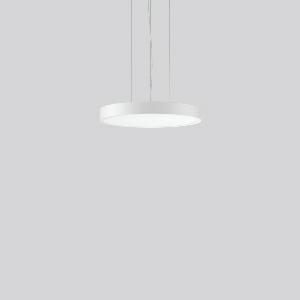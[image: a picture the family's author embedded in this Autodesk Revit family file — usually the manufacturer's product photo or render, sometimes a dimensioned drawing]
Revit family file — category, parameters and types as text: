
# Revit family: triona_round_p_312422_002_730_0688
name_source: partatom
category: Lighting Fixtures
units: mm (PartAtom-declared; Revit-internal decimal feet)

## family parameters
Cut with Voids When Loaded = No
Host = Face
Light Source = No
Part Type = Normal
Room Calculation Point = No
Round Connector Dimension = Use Diameter
Shared = No

## types (1)
- TRIONA round P (1 x LED Modul 830, 5850 lm, 3000)
    Apparent Load = 64 VA
    CIE Flux Codes = 49 80 96 82 100
    Color Rendering = 80
    Color Temperature = 3000
    Default Elevation = 1800 mm
    Description = Series: TRIONA round
Decorative round LED pendant-mounted surface luminaire. Flat, seamless frame: aluminium extrusion profile, powder coated. Cover made of sheet steel, powder-coated. Canopy made of aluminium, powder-coated. Direct light emission through a diffuser plastic opal. Indirect light emission through a flush diffuser made of satin-finish plastic. Lightguide and diffuser made of non-yellowing plastic (PMMA). Lateral light emission (RZB SIDELITE technology) for above-average homogeneous light distribution. Direct 70%, indirect 30% light emission. 3-point steel cable suspension, steplessly adjustable. Easy installation with transparent, adjustable pendant cable and canopy with magnetic fixing. Driver integrated. 
Colour: traffic white, matt (RAL 9016)
Diameter: 461 mm
Height: 52 mm
Suspension length: 500-1200 mm
Lamp: LED
Socket: without socket
Colour temperature: 3000K
Colour rendering index (CRI): 80
System power: 64 W
Rated luminous flux: 5850 lm
Luminous efficiency: 91 lm/W
Control gear: Dimmable Bluetooth converter
Protection class: I
Type of protection: IP 20
    Height = 52 mm  [stored 0.170604 ft]
    Lamp = 1 x LED Modul 830
    Lamp Light Flux = 5850 lm
    Lamp count = 1
    Length = 461 mm
    Lifetime = 50000 h
    Luminous efficacy = 91 lm/W
    Manufacturer = RZB
    ModVariant = No
    Model = 312422.002.730
    Mounting Place = Ceiling
    Mounting Type = Pendant
    Number of Poles = 1
    OnlyDefault = Yes
    Power Factor = 1
    Product Name = TRIONA round P
    Product group = Pendant modular luminaires
    ProductGroupID = 906
    Protection Class = Protection class I
    Protection Degree = IP 20
    RLX_Detail_Level = 1
    RLX_Emergency_Light_Flux = 0 lm
    RLX_Emergency_Type = 0
    RLX_Emergency_Type_DB = No
    RlxData = <blob elided: 32073 chars, md5=b4174391>
    Socket = socket
    Standby Power = 0 W
    System Light Flux = 5850 lm
    System Power = 64 W
    Type Comments = Product without accessories
    Type Image = 312422.002.jpg
    URL = http://relux.com
    VarID = ---
    Voltage = 230 V
    Voltage Range = 220-240 V
    Weight = 0.00 kg
    Width = 0 mm  [stored 0 ft]

note: [stored X ft] marks values corroborated as IEEE doubles in the binary element streams (Revit-internal decimal feet)

## geometry (parser evidence)
native form markers: Blend x4, Sweep x12
no freeform markers — native parametric forms only
